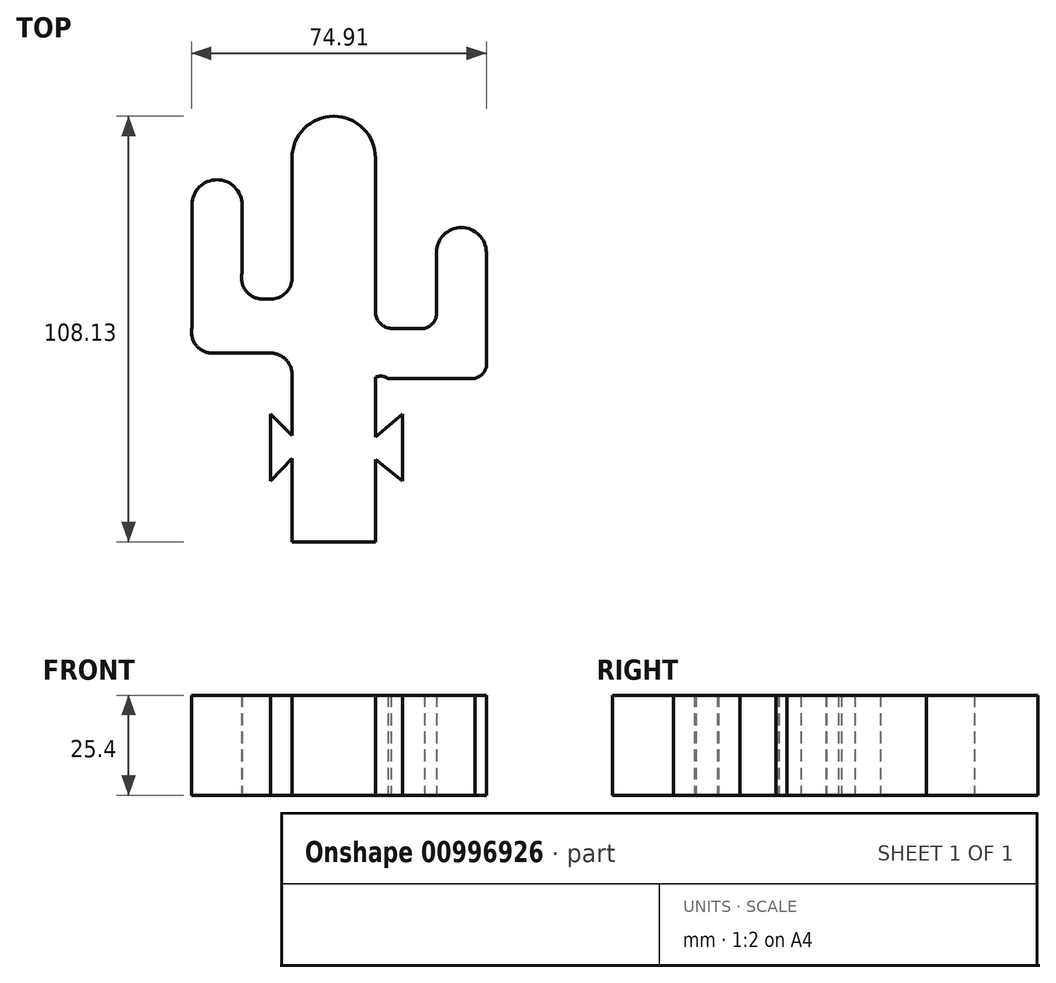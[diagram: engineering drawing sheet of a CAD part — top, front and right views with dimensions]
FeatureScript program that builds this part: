
annotation { "Feature Type Name" : "Feature", "Feature Type Description" : "" }
export const myFeature = defineFeature(function(context is Context, id is Id, definition is map)
    precondition{}
    {
        {
            var Q0;
            Q0=qCreatedBy(makeId("Top.planeOp"),FACE);
            var sketch = newSketch(context, id + "F0", { "sketchPlane" : qUnion([Q0])});
            skLineSegment(sketch, "E0", {"start": v(-21.22, 35.84) * mm, "end": v(-21.22, 5.36) * mm});
            skArc(sketch, "E1", {"start": v(0, 35.84) * mm, "mid": v(-10.6, 46.45) * mm, "end": v(-21.22, 35.84) * mm});
            skArc(sketch, "E2", {"start": v(-26.58, 0) * mm, "mid": v(-22.79, 1.57) * mm, "end": v(-21.22, 5.36) * mm});
            skLineSegment(sketch, "E3", {"start": v(-26.58, 0) * mm, "end": v(-28.67, 0) * mm});
            skArc(sketch, "E4", {"start": v(-33.92, 6.5) * mm, "mid": v(-32.85, 2) * mm, "end": v(-28.67, 0) * mm});
            skLineSegment(sketch, "E5", {"start": v(-33.92, 6.5) * mm, "end": v(-33.92, 23.95) * mm});
            skArc(sketch, "E6", {"start": v(-33.92, 23.95) * mm, "mid": v(-40.27, 30.3) * mm, "end": v(-46.62, 23.95) * mm});
            skLineSegment(sketch, "E7", {"start": v(-46.62, 23.95) * mm, "end": v(-46.62, -7.26) * mm});
            skArc(sketch, "E8", {"start": v(-46.62, -7.26) * mm, "mid": v(-45.55, -11.76) * mm, "end": v(-41.37, -13.75) * mm});
            skLineSegment(sketch, "E9", {"start": v(-41.37, -13.75) * mm, "end": v(-26.58, -13.75) * mm});
            skArc(sketch, "E10", {"start": v(-21.22, -19.3) * mm, "mid": v(-22.72, -15.39) * mm, "end": v(-26.58, -13.75) * mm});
            skLineSegment(sketch, "E11", {"start": v(-21.22, -19.3) * mm, "end": v(-21.22, -34.69) * mm});
            skLineSegment(sketch, "E12", {"start": v(0, 35.84) * mm, "end": v(0, -3.52) * mm});
            skLineSegment(sketch, "E13", {"start": v(3.99, -7.43) * mm, "end": v(12.48, -7.43) * mm});
            skLineSegment(sketch, "E14", {"start": v(15.47, -4.2) * mm, "end": v(15.47, 11.8) * mm});
            skLineSegment(sketch, "E15", {"start": v(28.17, 11.8) * mm, "end": v(28.17, -17.28) * mm});
            skLineSegment(sketch, "E16", {"start": v(25.33, -20.13) * mm, "end": v(3.15, -20.13) * mm});
            skLineSegment(sketch, "E17", {"start": v(0, -19.82) * mm, "end": v(0, -35) * mm});
            skLineSegment(sketch, "E18", {"start": v(0, -61.68) * mm, "end": v(-21.22, -61.68) * mm});
            skArc(sketch, "E19", {"start": v(28.17, 11.8) * mm, "mid": v(21.82, 18.16) * mm, "end": v(15.47, 11.8) * mm});
            skArc(sketch, "E20", {"start": v(12.48, -7.43) * mm, "mid": v(14.46, -6.26) * mm, "end": v(15.47, -4.2) * mm});
            skArc(sketch, "E21", {"start": v(23.3, -20.13) * mm, "mid": v(26.33, -19.72) * mm, "end": v(28.17, -17.28) * mm});
            skArc(sketch, "E22", {"start": v(0, -3.52) * mm, "mid": v(1.24, -6.24) * mm, "end": v(3.99, -7.43) * mm});
            skArc(sketch, "E23", {"start": v(3.15, -20.13) * mm, "mid": v(1.61, -19.6) * mm, "end": v(0, -19.82) * mm});
            skPoint(sketch, "E24.orphan", {"position": v(0, -20.13) * mm});
            skLineSegment(sketch, "E25", {"start": v(-21.22, -34.69) * mm, "end": v(-26.7, -29.23) * mm});
            skLineSegment(sketch, "E26", {"start": v(-26.7, -29.23) * mm, "end": v(-26.7, -46.2) * mm});
            skLineSegment(sketch, "E27", {"start": v(-26.7, -46.2) * mm, "end": v(-21.22, -40.49) * mm});
            skLineSegment(sketch, "E28", {"start": v(0, -40.75) * mm, "end": v(6.89, -46.2) * mm});
            skLineSegment(sketch, "E29", {"start": v(6.89, -46.2) * mm, "end": v(6.89, -29.23) * mm});
            skLineSegment(sketch, "E30", {"start": v(6.89, -29.23) * mm, "end": v(0, -35) * mm});
            skLineSegment(sketch, "E31", {"start": v(-21.22, -34.69) * mm, "end": v(0, -35) * mm, "construction": true});
            skLineSegment(sketch, "E32", {"start": v(-21.22, -40.49) * mm, "end": v(0, -40.75) * mm, "construction": true});
            skLineSegment(sketch, "E33.trimOffspring", {"start": v(0, -40.75) * mm, "end": v(0, -61.68) * mm});
            skLineSegment(sketch, "E34.trimOffspring", {"start": v(-21.22, -40.49) * mm, "end": v(-21.22, -61.68) * mm});
            skLineSegment(sketch, "E35", {"start": v(-26.7, -29.23) * mm, "end": v(6.89, -29.23) * mm, "construction": true});
            skLineSegment(sketch, "E36", {"start": v(-26.7, -46.2) * mm, "end": v(6.89, -46.2) * mm, "construction": true});
            skSolve(sketch);
        }
        {
            var Q0;
            Q0=makeQuery(id+"F0.imprint","IMPRINT",FACE,{"disambiguationData":[TD([[makeQuery(id+"F0.imprint","IMPRINT",EDGE,{"derivedFrom":sQuery(id+"F0.wireOp",EDGE,"E0")}),1.0]])]});
            extrude(context, id + "F1", {"entities" : qUnion([Q0]), "depth" : 25.4 * mm, "offsetDistance" : 25.4 * mm});
        }
    });
